# Revit family: Internal block_22_71_W
name_source: partatom
category: Оборудование
units: mm (PartAtom-declared; Revit-internal decimal feet)

## family parameters
Всегда вертикально = Да
Классификация = Нет
На основе рабочей плоскости = Нет
Общий = Нет
При загрузке вырезать с полостями = Нет
Размер круглого соединителя = Использовать диаметр
Тип детали = Нормальный
Точка принадлежности помещению = Нет

## types (6) — shared parameters
00_20_Manufacturer = BLAUBERG
00_20_Name = Internal block
Casing Material = Plastic white
Grid Material = Mesh, steel, painted,  white
Height = 870 мм
Length = 1150 мм
Load Classification = HVAC
Maintenance zone material = <По категории>
Maximum Air Flow = 0.0 л/с
Width = 528 мм
Изготовитель = BLAUBERG
zero-valued in all types: Отметка по умолчанию

## per-type parameters (varying)
| type | A | B | C | Power | Weight | r | r1 |
| BLHV-22-I-W-DC/1R1A | 864 мм | 300 мм | 200 мм | 150 Вт | 9.50 кг | 40 мм | 200 мм |
| BLHV-45-I-W-DC/1R1A | 972 мм | 320 мм | 215 мм | 200 Вт | 11.50 кг | 60 мм | 300 мм |
| BLHV-28-I-W-DC/1R1 | 864 мм | 300 мм | 200 мм | 150 Вт | 9.50 кг | 40 мм | 200 мм |
| BLHV-36-I-W-DC/1R1A | 864 мм | 300 мм | 200 мм | 180 Вт | 9.50 кг | 40 мм | 200 мм |
| BLHV-56-I-W-DC/1R1A | 972 мм | 320 мм | 215 мм | 230 Вт | 11.50 кг | 60 мм | 300 мм |
| BLHV-71-I-W-DC/1R1A | 972 мм | 320 мм | 215 мм | 350 Вт | 11.50 кг | 60 мм | 300 мм |

note: column(s) folded — value = type name in every type: 00_20_Type
